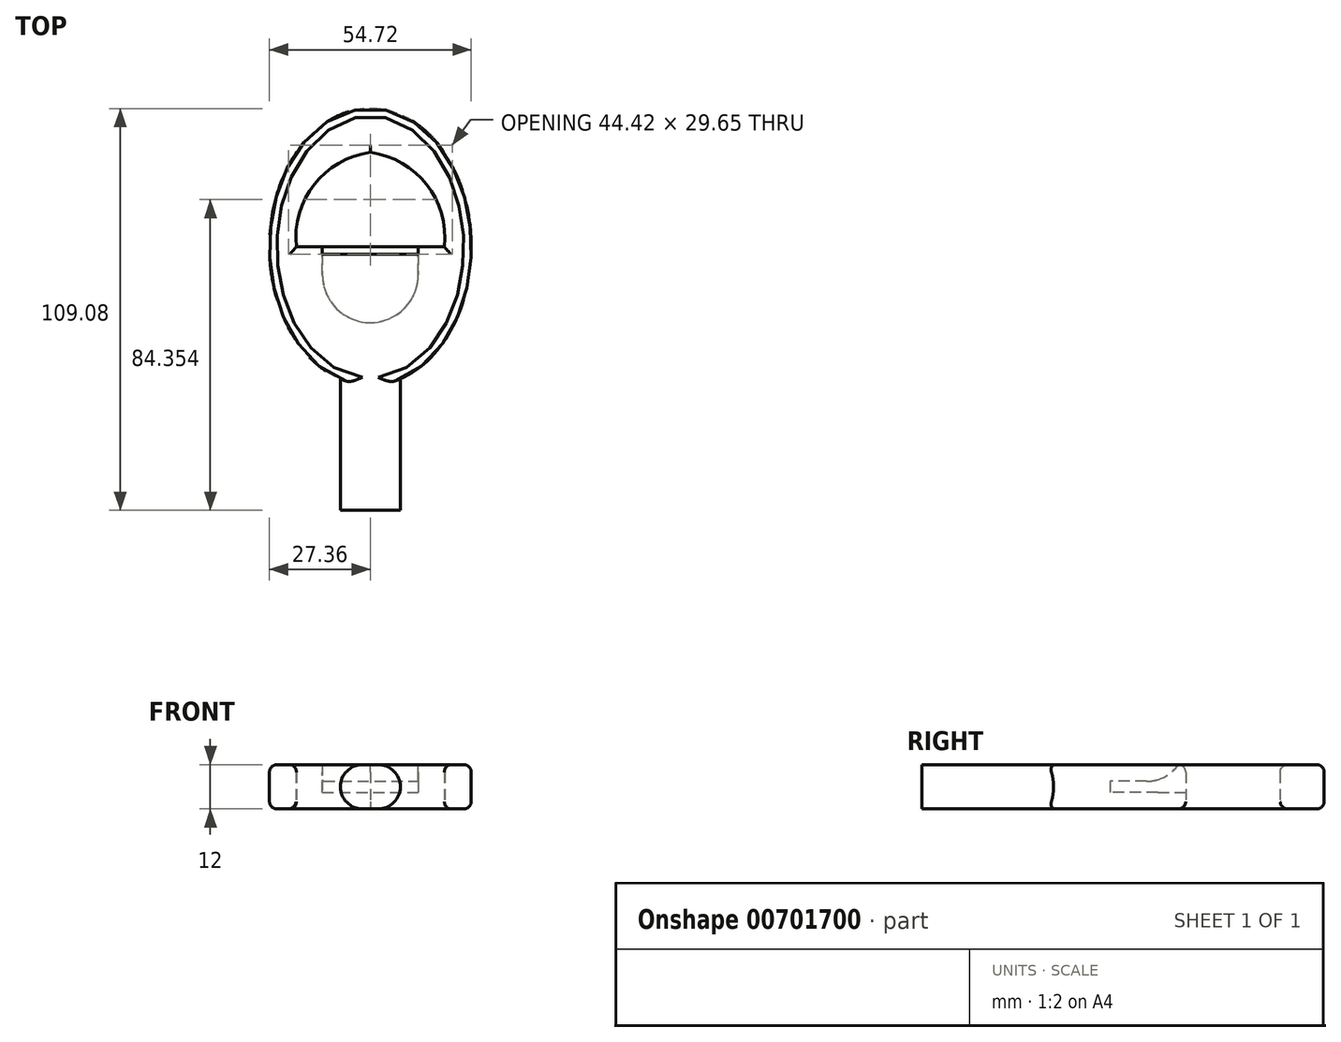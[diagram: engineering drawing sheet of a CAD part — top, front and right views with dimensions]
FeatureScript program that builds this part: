
annotation { "Feature Type Name" : "Feature", "Feature Type Description" : "" }
export const myFeature = defineFeature(function(context is Context, id is Id, definition is map)
    precondition{}
    {
        {
            var Q0;
            Q0=qCreatedBy(makeId("Top.planeOp"),FACE);
            var sketch = newSketch(context, id + "F0", { "sketchPlane" : qUnion([Q0])});
            skEllipse(sketch, "E0", {"center": v(0, 0) * mm, "majorRadius": 37.55 * mm, "minorRadius": 27.36 * mm, "majorAxis": v(0, -1)});
            skLineSegment(sketch, "E1.bottom", {"start": v(-8.14, 0) * mm, "end": v(8.14, 0) * mm});
            skLineSegment(sketch, "E1.top", {"start": v(-8.14, -71.53) * mm, "end": v(8.14, -71.53) * mm});
            skLineSegment(sketch, "E1.left", {"start": v(-8.14, 0) * mm, "end": v(-8.14, -71.53) * mm});
            skLineSegment(sketch, "E1.right", {"start": v(8.14, 0) * mm, "end": v(8.14, -71.53) * mm});
            skArc(sketch, "E2", {"start": v(0, 25.63) * mm, "mid": v(-15.26, 16.9) * mm, "end": v(-20.08, 0) * mm});
            skLineSegment(sketch, "E3", {"start": v(-20.08, 0) * mm, "end": v(0, 0) * mm});
            skArc(sketch, "E4.MirrorCS", {"start": v(0, 25.63) * mm, "mid": v(15.26, 16.9) * mm, "end": v(20.08, 0) * mm});
            skLineSegment(sketch, "E5.MirrorCS", {"start": v(20.08, 0) * mm, "end": v(0, 0) * mm});
            skSolve(sketch);
        }
        {
            var Q0;
            Q0=makeQuery(id+"F0.imprint","IMPRINT",FACE,{"disambiguationData":[TD([[makeQuery(id+"F0.imprint","IMPRINT",EDGE,{"derivedFrom":sQuery(id+"F0.wireOp",EDGE,"7f6qdyD0-leLh-K5xR-HI9C-ABOgbyIXevNR")}),1.0]])]});
            var Q1;
            {var subQ0=sQuery(id+"F0.wireOp",EDGE,"E2");Q1=makeQuery(id+"F0.imprint","IMPRINT",FACE,{"disambiguationData":[TD([[makeQuery(id+"F0.imprint","IMPRINT",EDGE,{"derivedFrom":subQ0}),-1.0]])]});}
            var Q2;
            {var subQ1=sQuery(id+"F0.wireOp",EDGE,"E1.left");var subQ7=sQuery(id+"F0.wireOp",EDGE,"E0");var subQ9=makeQuery(id+"F0.imprint","INTERSECT",VERTEX,{"derivedFrom":[subQ7,subQ1]});Q2=makeQuery(id+"F0.imprint","IMPRINT",FACE,{"disambiguationData":[TD([[makeQuery(id+"F0.imprint","IMPRINT",EDGE,{"disambiguationData":[TD([[subQ9,-1.0]])],"derivedFrom":subQ7}),1.0]])]});}
            var Q3;
            {var subQ5=sQuery(id+"F0.wireOp",EDGE,"E1.top");Q3=makeQuery(id+"F0.imprint","IMPRINT",FACE,{"disambiguationData":[TD([[makeQuery(id+"F0.imprint","IMPRINT",EDGE,{"derivedFrom":subQ5}),1.0]])]});}
            extrude(context, id + "F1", {"entities" : qUnion([Q0, Q1, Q2, Q3]), "endBound" : BoundingType.SYMMETRIC, "depth" : 12 * mm, "offsetDistance" : 25 * mm});
        }
        {
            var Q0;
            Q0=qCreatedBy(makeId("Top.planeOp"),FACE);
            var sketch = newSketch(context, id + "F2", { "sketchPlane" : qUnion([Q0])});
            skCircle(sketch, "E6", {"center": v(0, 8.45) * mm, "radius": 13 * mm});
            skCircle(sketch, "E7", {"center": v(0, -7.55) * mm, "radius": 13 * mm});
            skLineSegment(sketch, "E8", {"start": v(-13, -7.55) * mm, "end": v(-13, 8.45) * mm});
            skLineSegment(sketch, "E9", {"start": v(13, 8.45) * mm, "end": v(13, -7.55) * mm});
            skSolve(sketch);
        }
        {
            var Q0;
            Q0 = qSketchRegion(id + "F2", true);
            var Q1;
            {var subQ0=sQuery(id+"F2.wireOp",EDGE,"E7");var subQ1=sQuery(id+"F2.wireOp",EDGE,"E6");var subQ2=makeQuery(id+"F2.imprint","INTERSECT",VERTEX,{"disambiguationData":[OD(0.0)],"derivedFrom":[subQ1,subQ0]});Q1=makeQuery(id+"F2.imprint","IMPRINT",FACE,{"disambiguationData":[TD([[makeQuery(id+"F2.imprint","IMPRINT",EDGE,{"disambiguationData":[TD([[subQ2,-1.0]])],"derivedFrom":subQ1}),1.0]])]});}
            extrude(context, id + "F3", {"entities" : qUnion([Q0, Q1]), "operationType" : NewBodyOperationType.REMOVE, "endBound" : BoundingType.SYMMETRIC, "depth" : 3 * mm, "offsetDistance" : 25 * mm});
        }
        {
            var Q0;
            Q0=makeQuery(id+"F1.opExtrude","CAP_EDGE",EDGE,{"disambiguationData":[OSD([sQuery(id+"F0.wireOp",EDGE,"E1.left")])],"isStart":false});
            var Q1;
            Q1=makeQuery(id+"F1.opExtrude","CAP_EDGE",EDGE,{"disambiguationData":[OSD([sQuery(id+"F0.wireOp",EDGE,"E1.right")])],"isStart":false});
            var Q2;
            Q2=makeQuery(id+"F1.opExtrude","CAP_EDGE",EDGE,{"disambiguationData":[OSD([sQuery(id+"F0.wireOp",EDGE,"E1.left")])],"isStart":true});
            var Q3;
            Q3=makeQuery(id+"F1.opExtrude","CAP_EDGE",EDGE,{"disambiguationData":[OSD([sQuery(id+"F0.wireOp",EDGE,"E1.right")])],"isStart":true});
            fillet(context, id + "F4", {"entities" : qUnion([Q0, Q1, Q2, Q3]), "radius" : 6 * mm, "tangentPropagation" : true, "allowEdgeOverflow" : false});
        }
        {
            var Q0;
            Q0=makeQuery(id+"F1.opExtrude","CAP_EDGE",EDGE,{"disambiguationData":[OSD([sQuery(id+"F0.wireOp",EDGE,"E0")])],"isStart":false});
            var Q1;
            Q1=makeQuery(id+"F1.opExtrude","CAP_EDGE",EDGE,{"disambiguationData":[OSD([sQuery(id+"F0.wireOp",EDGE,"E0")])],"isStart":true});
            var Q2;
            Q2=makeQuery(id+"F1.opExtrude","CAP_EDGE",EDGE,{"disambiguationData":[OSD([sQuery(id+"F0.wireOp",EDGE,"E3"),sQuery(id+"F0.wireOp",EDGE,"E5.MirrorCS")])],"isStart":false});
            var Q3;
            Q3=makeQuery(id+"F1.opExtrude","CAP_EDGE",EDGE,{"disambiguationData":[OSD([sQuery(id+"F0.wireOp",EDGE,"E3"),sQuery(id+"F0.wireOp",EDGE,"E5.MirrorCS")])],"isStart":true});
            fillet(context, id + "F5", {"entities" : qUnion([Q0, Q1, Q2, Q3]), "radius" : 2 * mm, "tangentPropagation" : true, "allowEdgeOverflow" : false});
        }
        {
            var Q0;
            Q0=makeQuery(id+"F3.boolean.opBoolean","INTERSECT",EDGE,{"derivedFrom":[makeQuery(id+"F1.opExtrude","SWEPT_FACE",FACE,{"disambiguationData":[OSD([sQuery(id+"F0.wireOp",EDGE,"E3"),sQuery(id+"F0.wireOp",EDGE,"E5.MirrorCS")])]}),makeQuery(id+"F3.opExtrude","CAP_FACE",FACE,{"disambiguationData":[OSD([sQuery(id+"F2.wireOp",EDGE,"E6"),sQuery(id+"F2.wireOp",EDGE,"E7"),sQuery(id+"F2.wireOp",EDGE,"E8"),sQuery(id+"F2.wireOp",EDGE,"E9")])],"isStart":false})]});
            fillet(context, id + "F6", {"entities" : qUnion([Q0]), "radius" : 10.62 * mm, "tangentPropagation" : true, "allowEdgeOverflow" : false});
        }
        {
            var Q0;
            Q0=makeQuery(id+"F1.opExtrude","CAP_EDGE",EDGE,{"disambiguationData":[OSD([sQuery(id+"F0.wireOp",EDGE,"E4.MirrorCS")])],"isStart":false});
            var Q1;
            Q1=makeQuery(id+"F1.opExtrude","CAP_EDGE",EDGE,{"disambiguationData":[OSD([sQuery(id+"F0.wireOp",EDGE,"E2")])],"isStart":false});
            var Q2;
            Q2=makeQuery(id+"F1.opExtrude","CAP_EDGE",EDGE,{"disambiguationData":[OSD([sQuery(id+"F0.wireOp",EDGE,"E4.MirrorCS")])],"isStart":true});
            var Q3;
            Q3=makeQuery(id+"F1.opExtrude","CAP_EDGE",EDGE,{"disambiguationData":[OSD([sQuery(id+"F0.wireOp",EDGE,"E2")])],"isStart":true});
            fillet(context, id + "F7", {"entities" : qUnion([Q0, Q1, Q2, Q3]), "radius" : 2 * mm, "tangentPropagation" : true, "allowEdgeOverflow" : false});
        }
    });
